# Revit family: Layout-Teknion-Zones_Hinged_Screen_01-R2020
name_source: partatom
category: Furniture Systems
units: mm (PartAtom-declared; Revit-internal decimal feet)

## family parameters
Always vertical = Yes
Cut with Voids When Loaded = No
OmniClass Number = 23.40.70.14.64.21
OmniClass Title = Systems Furniture
Part Type = Normal
Room Calculation Point = No
Round Connector Dimension = Use Diameter
Shared = Yes
Work Plane-Based = No

## types (1)
- Layout 1
    Assembly Code = E2020200
    Default Elevation = 0' - 0"
    Depth = 0' - 0"
    Description = 9'-8" x 21'-4" Overall
    Height = 2' - 5"
    Keynote = Layout 01
    Length = 0' - 0"
    Manufacturer = Teknion
    Manufacturer Fax = 416.661.4586
    Model = "Zones Hinged Screen 01 Layout"
    Product Line = Zones
    Product Page URL = https://www.teknionplanningtool.com
    Series = Zones
    Sustainability Data = https://www.teknion.com
    URL = www.teknion.com
    Unit Weight URL = http://www.teknion.com
    Warranty = http://www.teknion.com
    Width = 0' - 0"

## geometry (parser evidence)
native form markers: Blend x14, Sweep x49
no freeform markers — native parametric forms only
